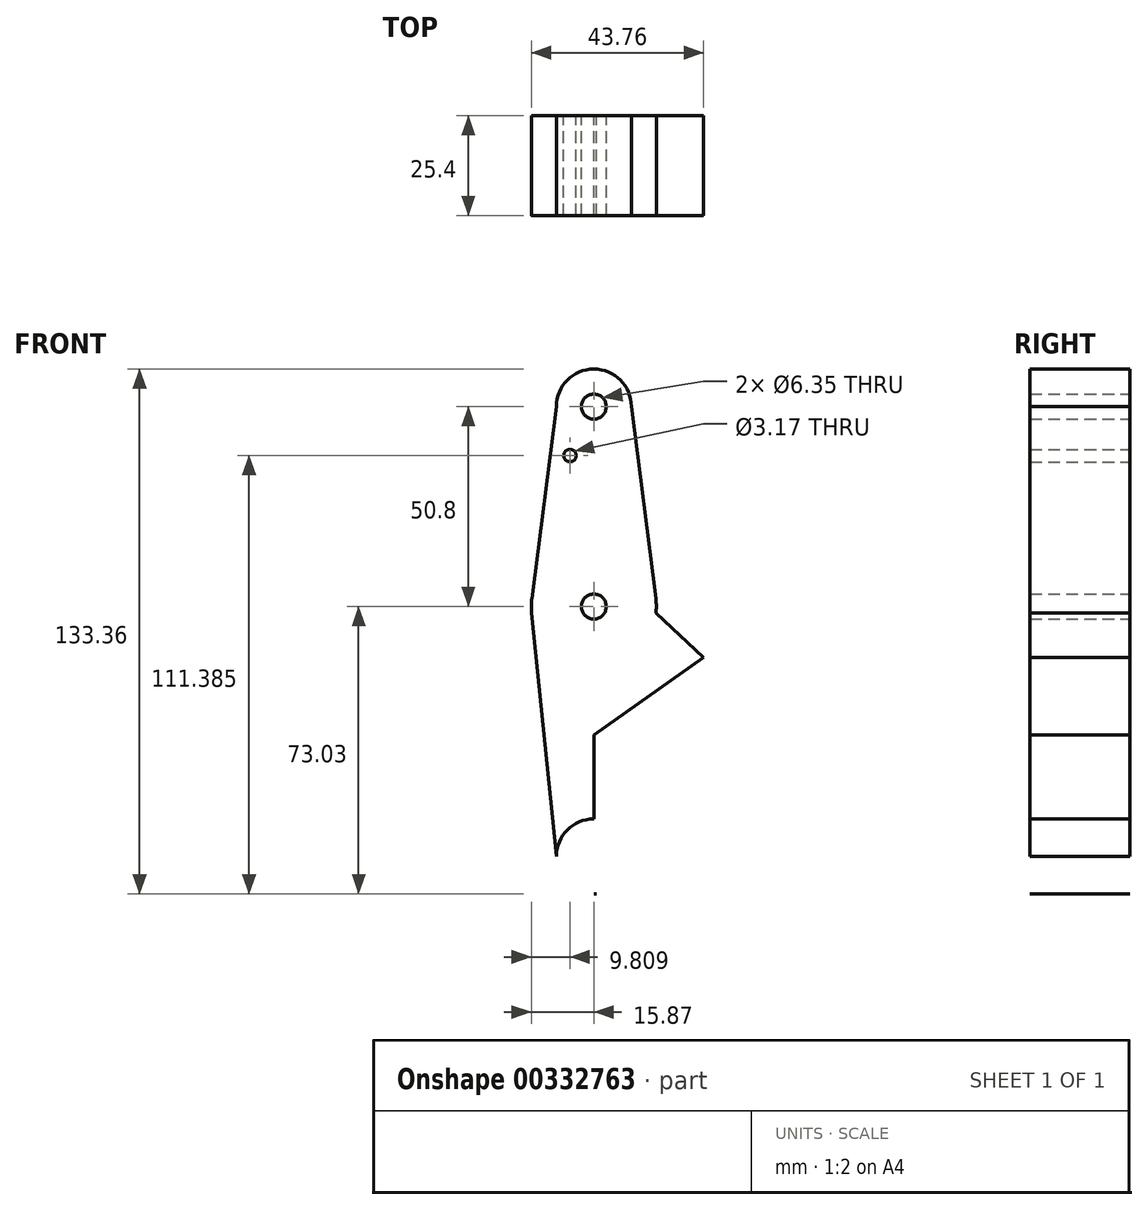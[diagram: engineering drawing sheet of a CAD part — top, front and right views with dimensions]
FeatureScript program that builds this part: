
annotation { "Feature Type Name" : "Feature", "Feature Type Description" : "" }
export const myFeature = defineFeature(function(context is Context, id is Id, definition is map)
    precondition{}
    {
        {
            var Q0;
            Q0=qCreatedBy(makeId("Front.planeOp"),FACE);
            var sketch = newSketch(context, id + "F0", { "sketchPlane" : qUnion([Q0])});
            skLineSegment(sketch, "E0", {"start": v(0, 0) * mm, "end": v(0, 114.3) * mm});
            skLineSegment(sketch, "E1", {"start": v(0, 114.3) * mm, "end": v(0, 0) * mm, "construction": true});
            skLineSegment(sketch, "E2", {"start": v(0, 0) * mm, "end": v(3.17, 0) * mm, "construction": true});
            skCircle(sketch, "E3", {"center": v(0, 114.3) * mm, "radius": 9.53 * mm});
            skArc(sketch, "E4", {"start": v(0, 9.53) * mm, "mid": v(-6.74, -6.74) * mm, "end": v(9.53, 0) * mm});
            skArc(sketch, "E5", {"start": v(44.73, -7.93) * mm, "mid": v(44.73, -7.93) * mm, "end": v(44.73, -7.93) * mm});
            skCircle(sketch, "E6", {"center": v(0, 63.5) * mm, "radius": 15.88 * mm});
            skLineSegment(sketch, "E7", {"start": v(-9.53, 114.3) * mm, "end": v(-15.75, 65.5) * mm});
            skLineSegment(sketch, "E8", {"start": v(-9.53, 0) * mm, "end": v(-15.8, 61.9) * mm});
            skLineSegment(sketch, "E9", {"start": v(-15.8, 61.9) * mm, "end": v(-9.53, 0) * mm});
            skLineSegment(sketch, "E10", {"start": v(0, -9.53) * mm, "end": v(0.68, -9.5) * mm});
            skLineSegment(sketch, "E11", {"start": v(9.53, 114.3) * mm, "end": v(15.75, 65.5) * mm});
            skLineSegment(sketch, "E12", {"start": v(15.75, 61.9) * mm, "end": v(27.9, 50.5) * mm});
            skCircle(sketch, "E13", {"center": v(0, 114.3) * mm, "radius": 3.18 * mm});
            skCircle(sketch, "E14", {"center": v(0, 63.5) * mm, "radius": 3.18 * mm});
            skCircle(sketch, "E15", {"center": v(-6.06, 101.86) * mm, "radius": 1.59 * mm});
            skPoint(sketch, "E16.newPointB", {"position": v(0, 9.52) * mm});
            skArc(sketch, "E16.filletArc", {"start": v(72.2, 8.92) * mm, "mid": v(74.58, 7.38) * mm, "end": v(77.35, 6.77) * mm});
            skLineSegment(sketch, "E17", {"start": v(22.22, 14.72) * mm, "end": v(22.41, 55.64) * mm});
            skLineSegment(sketch, "E18", {"start": v(44.73, -7.93) * mm, "end": v(44.73, -7.93) * mm});
            skPoint(sketch, "E19", {"position": v(22.23, 0) * mm});
            skLineSegment(sketch, "E20.trimOffspring", {"start": v(-11.82, 22.64) * mm, "end": v(27.9, 50.5) * mm});
            skPoint(sketch, "E21.start.orphan", {"position": v(-59.75, -7.62) * mm});
            skPoint(sketch, "E22.end.orphan", {"position": v(-59.75, -9.53) * mm});
            skPoint(sketch, "E23.end.orphan", {"position": v(131.96, 119.3) * mm});
            skPoint(sketch, "E23.start.orphan", {"position": v(125.94, 119.3) * mm});
            skPoint(sketch, "E24.orphan", {"position": v(18.2, 6.77) * mm});
            skLineSegment(sketch, "E25.trimOffspring", {"start": v(9.52, 0) * mm, "end": v(22.23, 0) * mm, "construction": true});
            skPoint(sketch, "E26.orphan", {"position": v(44.73, 7.93) * mm});
            skSolve(sketch);
        }
        {
            var Q0;
            Q0 = qSketchRegion(id + "F0", true);
            extrude(context, id + "F1", {"entities" : qUnion([Q0]), "flatOperationType" : FlatOperationType.REMOVE, "offsetDistance" : 25.4 * mm, "depth" : 25.4 * mm, "domain" : OperationDomain.MODEL});
        }
    });
